# Revit family: Keilhauer-GSD-5_star_Base_Chair-Aluminum-
name_source: partatom
category: Furniture
revit_build: Autodesk Revit 2016 (Build: 20150220_1215(x64)
units: mm (PartAtom-declared; Revit-internal decimal feet)

## family parameters
Always vertical = Yes
Cut with Voids When Loaded = No
OmniClass Number = 23.40.20.00
OmniClass Title = General Furniture and Specialties
Room Calculation Point = No
Shared = No
Work Plane-Based = No

## types (2) — shared parameters
Assembly Code = E2020200
Depth = 26"
Height = 32"
Keynote = 12500
Low Emitting Finish = Yes
Low Emitting Material = Yes
Manufacturer = Keilhauer
Product Documentation Link = https://keilhauer.com
Revit File Built By = https://servex-us.com
Salvage or Reuse = Yes
Type Comments = GSD
URL = https://keilhauer.com
Width = 26 1/2"
zero-valued in all types: Percentage of Recycled Content

## per-type parameters (varying)
| type | Description |
| 86120 | Side chair with ash arms, 5-star aluminum base |
| 86121 | Side chair with walnut arms, 5-star aluminum base |

note: column(s) folded — value = type name in every type: Model

## geometry (parser evidence)
native form markers: Sweep x9
no freeform markers — native parametric forms only
